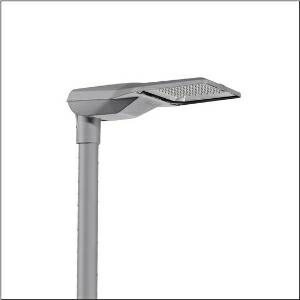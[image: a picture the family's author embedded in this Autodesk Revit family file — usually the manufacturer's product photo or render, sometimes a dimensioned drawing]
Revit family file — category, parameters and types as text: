
# Revit family: streetlight_sl_21_iq_midi___p0_8a_5xe3u31g08mb_ba97
name_source: partatom
category: Lighting Fixtures
units: mm (PartAtom-declared; Revit-internal decimal feet)

## family parameters
Cut with Voids When Loaded = No
Host = Face
Light Source = No
Part Type = Normal
Room Calculation Point = No
Round Connector Dimension = Use Diameter
Shared = No

## types (1)
- --- (1 x LED, 19670 lm, 146.7 W, 3000K)
    Apparent Load = 147 VA
    CIE Flux Codes = 33 69 96 100 100
    Color Rendering = 70
    Color Temperature = 3000K
    Default Elevation = 1800 mm
    Description = Streetlight SL 21 iQ midi, mast luminaire, primary light control with lens, of PMMA, primary optical cover: cover, of toughened safety glass, transparent, light distribution: P0.8a, light emission: direct distribution, primary light characteristic: asymmetric, installation type: post-top, side-entry, LED, High Power LED, rated luminous flux: 19.670lm, luminous efficacy: 134lm/W, light colour: 730, colour temperature: 3000K, control gear: iQ Street-Remote, control: pre-setting: linear dimming characteristic, Street-Remote, Auto-Match, Temp-Guard, Lumen-Switch, Night-Set, Smart-Wire, Light-Fading, Desk-Remote (wireless, voltage-free reading and setting of iQ features in the workshop via application-optimized NFC function/RFID function), optimised constant luminous flux control (CLO 2.0), mains connection: 230..240V, AC, 50/60Hz, start of lifetime: 147W, end of service life: 161W, reduction: 62W, luminaire housing, of diecast aluminium, powder-coated, SITECO metallic grey (DB 702S), corrosivity category C5 high according to DIN EN ISO 12944, please order mast flange separately, inclination adjustable: 0°, 5°, 10°, 15°, sealing non-destructively replaceable, multi-level sealing system, length: 644mm, width: 335mm, height: 110mm, mast flange for spigot size: 42mm (side-entry): 5XC10008XM4, 60/48mm (side-entry/post-top): 5XC10108XM2, 76/60mm (side-entry/post-top): 5XC10108XM1, mounting height: 4..8m, protection rating (complete): IP66, insulation class (complete): insulation class II (safety insulation), certification: CE, ENEC, ENEC+, VDE, impact resistance: IK10, permissible operating ambient temperature for outdoor applications: -40..+50°C, standard-compliant lighting for roads and squares, packaging unit: 1 piece

Light Distribution: P0.8a
    Height = 111 mm
    Lamp = 1 x LED
    Lamp Light Flux = 19670 lm
    Lamp Power = 146.7 W
    Lamp count = 1
    Length = 644 mm
    Luminous efficacy = 134 lm/W
    Manufacturer = Siteco
    ModVariant = No
    Model = 5XE3U31G08MB
    Number of Poles = 1
    OnlyDefault = Yes
    Power Factor = 1
    Product Name = Streetlight SL 21 iQ midi | P0.8a
    Product group = mast luminaire | pylon top
    ProductGroupID = 6100
    Protection Class = Protection class II
    Protection Degree = IP 66
    RLX_Detail_Level = 1
    RLX_Emergency_Light_Flux = 0 lm
    RLX_Emergency_Type = 0
    RLX_Emergency_Type_DB = No
    RlxData = <blob elided: 90113 chars, md5=f5636c60>
    Socket = socket
    Standby Power = 0 W
    System Light Flux = 19670 lm
    System Power = 147 W
    Type Comments = factory setting: luminous flux: 100 % | dim-lin: 254 | 753 mA
    Type Image = l_1004298.jpg
    URL = http://relux.com
    VarID = @adj_080067
    Voltage = 0 V
    Weight = 0.00 kg
    Width = 336 mm

## geometry (parser evidence)
native form markers: Blend x4, Sweep x11
no freeform markers — native parametric forms only
